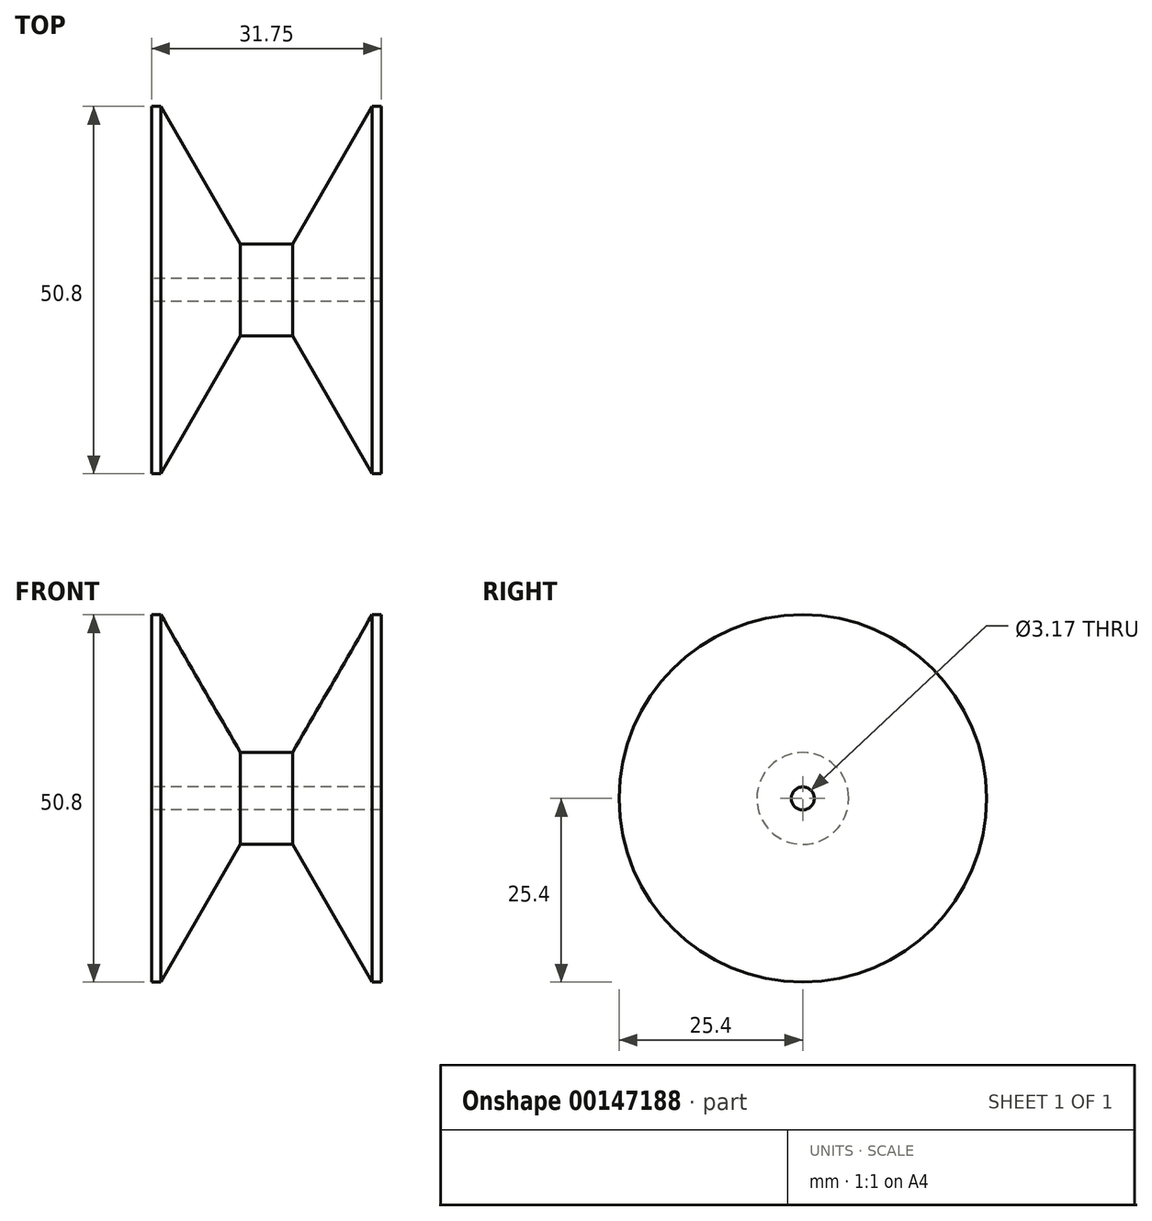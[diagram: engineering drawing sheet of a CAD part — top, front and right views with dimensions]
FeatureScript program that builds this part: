
annotation { "Feature Type Name" : "Feature", "Feature Type Description" : "" }
export const myFeature = defineFeature(function(context is Context, id is Id, definition is map)
    precondition{}
    {
        {
            var Q0;
            Q0=qCreatedBy(makeId("Front.planeOp"),FACE);
            var sketch = newSketch(context, id + "F0", { "sketchPlane" : qUnion([Q0])});
            skLineSegment(sketch, "E0", {"start": v(0, 0) * mm, "end": v(100.77, 0) * mm, "construction": true});
            skLineSegment(sketch, "E1", {"start": v(0, 1.59) * mm, "end": v(0, 25.4) * mm});
            skLineSegment(sketch, "E2", {"start": v(0, 25.4) * mm, "end": v(1.27, 25.4) * mm});
            skLineSegment(sketch, "E3", {"start": v(1.27, 25.4) * mm, "end": v(12.27, 6.35) * mm});
            skLineSegment(sketch, "E4", {"start": v(12.27, 6.35) * mm, "end": v(19.48, 6.35) * mm});
            skLineSegment(sketch, "E5", {"start": v(19.48, 6.35) * mm, "end": v(30.48, 25.4) * mm});
            skLineSegment(sketch, "E6", {"start": v(30.48, 25.4) * mm, "end": v(31.75, 25.4) * mm});
            skLineSegment(sketch, "E7", {"start": v(31.75, 25.4) * mm, "end": v(31.75, 1.59) * mm});
            skLineSegment(sketch, "E8", {"start": v(31.75, 1.59) * mm, "end": v(0, 1.59) * mm});
            skSolve(sketch);
        }
        {
            var Q0;
            Q0 = qSketchRegion(id + "F0", true);
            var Q1;
            Q1=sQuery(id+"F0.wireOp",EDGE,"E0");
            revolve(context, id + "F1", {"entities" : qUnion([Q0]), "axis" : qUnion([Q1]), "revolveType" : RevolveType.FULL});
        }
    });
